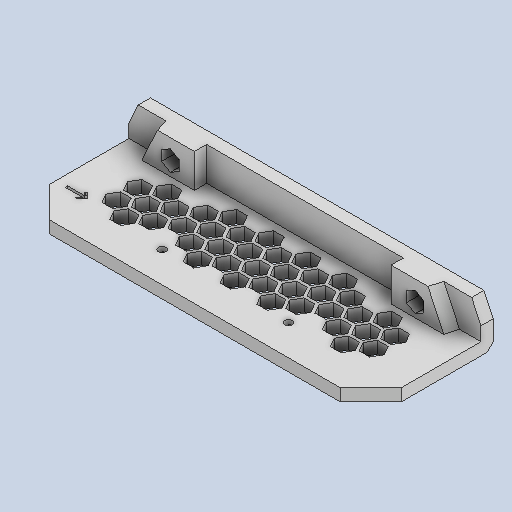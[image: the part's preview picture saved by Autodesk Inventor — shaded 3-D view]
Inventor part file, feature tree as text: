
AUTODESK INVENTOR PART (.ipt)
format: ipt  version: 2023 (Build 270158000, 158)  size: 689,664 bytes
history: native  units: mm
features: other x3, emboss x1, sketch x1, projected_geometry x1
ambient origin geometry x8: Origin, YZ Plane, XZ Plane, XY Plane, X Axis, Y Axis, Z Axis, Center Point
bodies: Solid1 (feature_tree)
feature tree (6):
  other  "A-01.ipt"
  emboss  "Emboss1"
  other  "Solid1::A-01.ipt"
  other  "TaggingFeature1"
  sketch  "Sketch3"  dims[d0=10.0mm d1=1.0mm d2=0.0mm]
  projected_geometry  "Projected Loop1"
